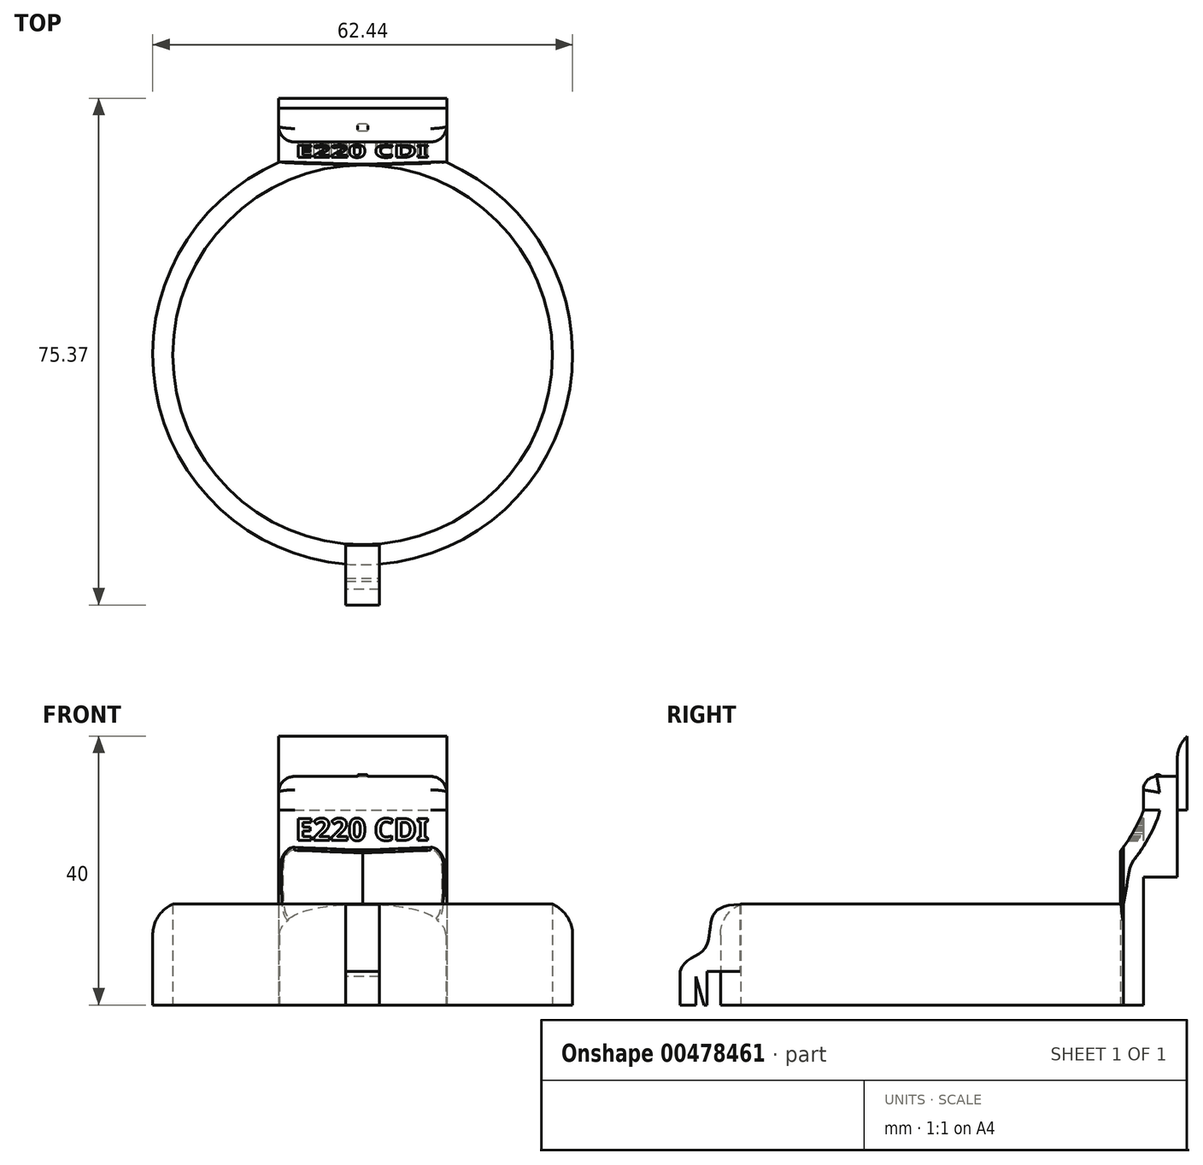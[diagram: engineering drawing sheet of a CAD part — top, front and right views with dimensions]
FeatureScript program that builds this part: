
annotation { "Feature Type Name" : "Feature", "Feature Type Description" : "" }
export const myFeature = defineFeature(function(context is Context, id is Id, definition is map)
    precondition{}
    {
        {
            var Q0;
            Q0=qCreatedBy(makeId("Top.planeOp"),FACE);
            var sketch = newSketch(context, id + "F0", { "sketchPlane" : qUnion([Q0])});
            skCircle(sketch, "E0", {"center": v(0, 0) * mm, "radius": 28.22 * mm});
            skCircle(sketch, "E1", {"center": v(0, 0) * mm, "radius": 31.22 * mm});
            skPoint(sketch, "E2", {"position": v(0, 31.22) * mm});
            skSolve(sketch);
        }
        {
            var Q0;
            Q0=makeQuery(id+"F0.imprint","IMPRINT",FACE,{"disambiguationData":[TD([[makeQuery(id+"F0.imprint","IMPRINT",EDGE,{"derivedFrom":sQuery(id+"F0.wireOp",EDGE,"E0")}),-1.0]])]});
            extrude(context, id + "F1", {"entities" : qUnion([Q0]), "depth" : 10 * mm, "hasSecondDirection" : true, "secondDirectionOppositeDirection" : true, "secondDirectionDepth" : 5 * mm});
        }
        {
            var Q0;
            Q0=qCreatedBy(makeId("Top.planeOp"),FACE);
            var sketch = newSketch(context, id + "F2", { "sketchPlane" : qUnion([Q0])});
            skLineSegment(sketch, "E3.bottom", {"start": v(-12.5, 31.66) * mm, "end": v(12.5, 31.66) * mm});
            skLineSegment(sketch, "E3.top", {"start": v(-12.5, 28.66) * mm, "end": v(12.5, 28.66) * mm});
            skLineSegment(sketch, "E3.left", {"start": v(-12.5, 31.66) * mm, "end": v(-12.5, 28.66) * mm});
            skLineSegment(sketch, "E3.right", {"start": v(12.5, 31.66) * mm, "end": v(12.5, 28.66) * mm});
            skLineSegment(sketch, "E4", {"start": v(-12.5, 31.66) * mm, "end": v(12.5, 28.66) * mm, "construction": true});
            skLineSegment(sketch, "E5", {"start": v(-12.5, 28.66) * mm, "end": v(12.5, 31.66) * mm, "construction": true});
            skPoint(sketch, "E6", {"position": v(0, 30.16) * mm});
            skSolve(sketch);
        }
        {
            var Q0;
            Q0=qSketchRegion(id+"F2",true);
            extrude(context, id + "F3", {"entities" : qUnion([Q0]), "operationType" : NewBodyOperationType.ADD, "depth" : 24 * mm, "hasSecondDirection" : true, "secondDirectionOppositeDirection" : true, "secondDirectionDepth" : 5 * mm});
        }
        {
            var Q0;
            Q0=makeQuery(id+"F3.opExtrude","CAP_FACE",FACE,{"disambiguationData":[OSD([sQuery(id+"F2.wireOp",EDGE,"E3.bottom"),sQuery(id+"F2.wireOp",EDGE,"E3.top"),sQuery(id+"F2.wireOp",EDGE,"E3.left"),sQuery(id+"F2.wireOp",EDGE,"E3.right")])],"isStart":false});
            var sketch = newSketch(context, id + "F4", { "sketchPlane" : qUnion([Q0])});
            skLineSegment(sketch, "E7.bottom", {"start": v(-12.5, 31.66) * mm, "end": v(12.5, 31.66) * mm});
            skLineSegment(sketch, "E7.top", {"start": v(-12.5, 36.66) * mm, "end": v(12.5, 36.66) * mm});
            skLineSegment(sketch, "E7.left", {"start": v(-12.5, 31.66) * mm, "end": v(-12.5, 36.66) * mm});
            skLineSegment(sketch, "E7.right", {"start": v(12.5, 31.66) * mm, "end": v(12.5, 36.66) * mm});
            skSolve(sketch);
        }
        {
            var Q0;
            Q0=qSketchRegion(id+"F4",true);
            extrude(context, id + "F5", {"entities" : qUnion([Q0]), "operationType" : NewBodyOperationType.ADD, "oppositeDirection" : true, "depth" : 10 * mm, "hasSecondDirection" : true, "secondDirectionOppositeDirection" : false, "secondDirectionDepth" : 5 * mm});
        }
        {
            var Q0;
            Q0=makeQuery(id+"F5.opExtrude","CAP_FACE",FACE,{"disambiguationData":[OSD([sQuery(id+"F4.wireOp",EDGE,"E7.bottom"),sQuery(id+"F4.wireOp",EDGE,"E7.top"),sQuery(id+"F4.wireOp",EDGE,"E7.left"),sQuery(id+"F4.wireOp",EDGE,"E7.right")])],"isStart":true});
            var sketch = newSketch(context, id + "F6", { "sketchPlane" : qUnion([Q0])});
            skLineSegment(sketch, "E8.bottom", {"start": v(-12.5, 36.66) * mm, "end": v(12.51, 36.66) * mm});
            skLineSegment(sketch, "E8.top", {"start": v(-12.5, 38.17) * mm, "end": v(12.51, 38.17) * mm});
            skLineSegment(sketch, "E8.left", {"start": v(-12.5, 36.66) * mm, "end": v(-12.5, 38.17) * mm});
            skLineSegment(sketch, "E8.right", {"start": v(12.51, 36.66) * mm, "end": v(12.51, 38.17) * mm});
            skSolve(sketch);
        }
        {
            var Q0;
            Q0=qCreatedBy(makeId("Right.planeOp"),FACE);
            var sketch = newSketch(context, id + "F7", { "sketchPlane" : qUnion([Q0])});
            skFitSpline(sketch, "E9", {"points": [v(-37.2, 0) * mm, v(-33.61, 3.33) * mm, v(-32.43, 8.1) * mm, v(-28.31, 9.98) * mm], "startDerivative": vector(3.1, 16.24) * mm, "endDerivative": vector(22.01, 0.89) * mm});
            skLineSegment(sketch, "E10", {"start": v(-28.31, 9.98) * mm, "end": v(-28.31, 0) * mm});
            skLineSegment(sketch, "E11", {"start": v(-28.31, 0) * mm, "end": v(-37.2, 0) * mm});
            skSolve(sketch);
        }
        {
            var Q0;
            Q0=makeQuery(id+"F7.imprint","IMPRINT",FACE,{"disambiguationData":[TD([[makeQuery(id+"F7.imprint","IMPRINT",EDGE,{"derivedFrom":sQuery(id+"F7.wireOp",EDGE,"E9")}),-1.0]])]});
            extrude(context, id + "F8", {"entities" : qUnion([Q0]), "depth" : 2.5 * mm, "hasSecondDirection" : true, "secondDirectionOppositeDirection" : true, "secondDirectionDepth" : 2.5 * mm});
        }
        {
            var Q0;
            Q0=qCreatedBy(makeId("Top.planeOp"),FACE);
            var sketch = newSketch(context, id + "F9", { "sketchPlane" : qUnion([Q0])});
            skLineSegment(sketch, "E12.bottom", {"start": v(-2.5, -37.2) * mm, "end": v(2.5, -37.2) * mm});
            skLineSegment(sketch, "E12.top", {"start": v(-2.5, -33.2) * mm, "end": v(2.5, -33.2) * mm});
            skLineSegment(sketch, "E12.left", {"start": v(-2.5, -37.2) * mm, "end": v(-2.5, -33.2) * mm});
            skLineSegment(sketch, "E12.right", {"start": v(2.5, -37.2) * mm, "end": v(2.5, -33.2) * mm});
            skSolve(sketch);
        }
        {
            var Q0;
            Q0=qSketchRegion(id+"F9",true);
            extrude(context, id + "F10", {"entities" : qUnion([Q0]), "operationType" : NewBodyOperationType.ADD, "oppositeDirection" : true, "depth" : 5 * mm});
        }
        {
            var Q0;
            {var subQ0=sQuery(id+"F0.wireOp",EDGE,"E1");var subQ1=sQuery(id+"F0.wireOp",EDGE,"E0");Q0=makeQuery(id+"F3.boolean.opBoolean","SPLIT",FACE,{"disambiguationData":[TD([makeQuery(id+"F1.opExtrude","SWEPT_FACE",FACE,{"disambiguationData":[OSD([subQ1])]})])],"derivedFrom":makeQuery(id+"F1.opExtrude","CAP_FACE",FACE,{"disambiguationData":[OSD([subQ1,subQ0])],"isStart":false})});}
            var sketch = newSketch(context, id + "F11", { "sketchPlane" : qUnion([Q0])});
            skFitSpline(sketch, "E13", {"points": [v(-12.37, 28.66) * mm, v(-7.02, 28.42) * mm, v(0, 28.22) * mm], "startDerivative": vector(16.95, -1.43) * mm, "endDerivative": vector(20.26, -0.24) * mm});
            skLineSegment(sketch, "E14", {"start": v(0, 28.22) * mm, "end": v(0, 28.66) * mm});
            skLineSegment(sketch, "E15", {"start": v(0, 28.66) * mm, "end": v(-12.37, 28.66) * mm});
            skFitSpline(sketch, "E16.MirrorCS", {"points": [v(12.37, 28.66) * mm, v(7.02, 28.42) * mm, v(0, 28.22) * mm], "startDerivative": vector(-16.95, -1.43) * mm, "endDerivative": vector(-20.26, -0.24) * mm});
            skLineSegment(sketch, "E17.MirrorCS", {"start": v(0, 28.66) * mm, "end": v(12.37, 28.66) * mm});
            skSolve(sketch);
        }
        {
            var Q0;
            Q0=qSketchRegion(id+"F11",true);
            extrude(context, id + "F12", {"entities" : qUnion([Q0]), "operationType" : NewBodyOperationType.ADD, "depth" : 14 * mm});
        }
        {
            var Q0;
            Q0=makeQuery(id+"F6.imprint","IMPRINT",FACE,{"disambiguationData":[TD([[makeQuery(id+"F6.imprint","IMPRINT",EDGE,{"derivedFrom":sQuery(id+"F6.wireOp",EDGE,"E8.top")}),-1.0]])]});
            extrude(context, id + "F13", {"entities" : qUnion([Q0]), "operationType" : NewBodyOperationType.ADD, "depth" : 6 * mm, "hasSecondDirection" : true, "secondDirectionOppositeDirection" : true, "secondDirectionDepth" : 5 * mm});
        }
        {
            var Q0;
            Q0=makeQuery(id+"F13.opExtrude","CAP_EDGE",EDGE,{"disambiguationData":[OSD([sQuery(id+"F6.wireOp",EDGE,"E8.bottom")])],"isStart":false});
            fillet(context, id + "F14", {"entities" : qUnion([Q0]), "radius" : 5 * mm, "tangentPropagation" : true, "allowEdgeOverflow" : false});
        }
        {
            var Q0;
            Q0=qCreatedBy(makeId("Right.planeOp"),FACE);
            var sketch = newSketch(context, id + "F15", { "sketchPlane" : qUnion([Q0])});
            skFitSpline(sketch, "E18", {"points": [v(31.66, 24) * mm, v(29.11, 19.07) * mm, v(27.3, 15.86) * mm, v(25.83, 10.1) * mm, v(23.5, 28.91) * mm, v(28.8, 25.36) * mm], "startDerivative": vector(-0.11, -8.56) * mm, "endDerivative": vector(26.45, -28.76) * mm});
            skLineSegment(sketch, "E19", {"start": v(28.8, 25.36) * mm, "end": v(31.66, 24) * mm});
            skSolve(sketch);
        }
        {
            var Q0;
            Q0 = qSketchRegion(id + "F15", true);
            extrude(context, id + "F16", {"entities" : qUnion([Q0]), "operationType" : NewBodyOperationType.REMOVE, "endBound" : BoundingType.THROUGH_ALL, "oppositeDirection" : true, "depth" : 25 * mm, "hasSecondDirection" : true, "secondDirectionBound" : SecondDirectionBoundingType.THROUGH_ALL, "secondDirectionOppositeDirection" : false, "secondDirectionDepth" : 25 * mm});
        }
        {
            var Q0;
            Q0=qCreatedBy(makeId("Right.planeOp"),FACE);
            var sketch = newSketch(context, id + "F17", { "sketchPlane" : qUnion([Q0])});
            skArc(sketch, "E20", {"start": v(34.37, 28.94) * mm, "mid": v(33.81, 29.28) * mm, "end": v(33.26, 28.94) * mm});
            skLineSegment(sketch, "E21", {"start": v(33.26, 28.94) * mm, "end": v(34.37, 28.94) * mm});
            skSolve(sketch);
        }
        {
            var Q0;
            Q0=makeQuery(id+"F17.imprint","IMPRINT",FACE,{"disambiguationData":[TD([[makeQuery(id+"F17.imprint","IMPRINT",EDGE,{"derivedFrom":sQuery(id+"F17.wireOp",EDGE,"E20")}),1.0]])]});
            var Q1;
            Q1 = qConstructionFilter(qBodyType(qCreatedBy(id + "F17" ,EDGE), BodyType.WIRE), ConstructionObject.NO);
            extrude(context, id + "F18", {"entities" : qUnion([Q0]), "surfaceEntities" : qUnion([Q1]), "endBound" : BoundingType.SYMMETRIC, "depth" : 1.5 * mm});
        }
        {
            var Q0;
            Q0=makeQuery(id+"F18.opExtrude","CAP_EDGE",EDGE,{"disambiguationData":[OSD([sQuery(id+"F17.wireOp",EDGE,"E20")])],"isStart":true});
            var Q1;
            Q1=makeQuery(id+"F18.opExtrude","CAP_EDGE",EDGE,{"disambiguationData":[OSD([sQuery(id+"F17.wireOp",EDGE,"E20")])],"isStart":false});
            fillet(context, id + "F19", {"entities" : qUnion([Q0, Q1]), "radius" : 0.22 * mm, "tangentPropagation" : true, "allowEdgeOverflow" : false});
        }
        {
            var Q0;
            Q0=makeQuery(id+"F5.opExtrude","CAP_EDGE",EDGE,{"disambiguationData":[OSD([sQuery(id+"F4.wireOp",EDGE,"E7.bottom")])],"isStart":true});
            fillet(context, id + "F20", {"entities" : qUnion([Q0]), "radius" : 2 * mm, "tangentPropagation" : true, "allowEdgeOverflow" : false});
        }
        {
            var Q0;
            Q0=makeQuery(id+"F16.boolean.opBoolean","INTERSECT",EDGE,{"derivedFrom":[makeQuery(id+"F5.boolean.opBoolean","MERGE",FACE,{"derivedFrom":[makeQuery(id+"F3.opExtrude","SWEPT_FACE",FACE,{"disambiguationData":[OSD([sQuery(id+"F2.wireOp",EDGE,"E3.right")])]}),makeQuery(id+"F5.opExtrude","SWEPT_FACE",FACE,{"disambiguationData":[OSD([sQuery(id+"F4.wireOp",EDGE,"E7.right")])]})]}),makeQuery(id+"F16.opExtrude","SWEPT_FACE",FACE,{"disambiguationData":[OSD([sQuery(id+"F15.wireOp",EDGE,"E18")])]})]});
            var Q1;
            Q1=makeQuery(id+"F5.opExtrude","SWEPT_EDGE",EDGE,{"disambiguationData":[OSD([sQuery(id+"F2.wireOp",EDGE,"E3.right"),sQuery(id+"F4.wireOp",EDGE,"E7.bottom"),sQuery(id+"F4.wireOp",EDGE,"E7.right")])]});
            var Q2;
            Q2=makeQuery(id+"F5.opExtrude","SWEPT_EDGE",EDGE,{"disambiguationData":[OSD([sQuery(id+"F2.wireOp",EDGE,"E3.left"),sQuery(id+"F4.wireOp",EDGE,"E7.bottom"),sQuery(id+"F4.wireOp",EDGE,"E7.left")])]});
            var Q3;
            Q3=makeQuery(id+"F16.boolean.opBoolean","INTERSECT",EDGE,{"derivedFrom":[makeQuery(id+"F13.boolean.opBoolean","MERGE",FACE,{"derivedFrom":[makeQuery(id+"F5.boolean.opBoolean","MERGE",FACE,{"derivedFrom":[makeQuery(id+"F3.opExtrude","SWEPT_FACE",FACE,{"disambiguationData":[OSD([sQuery(id+"F2.wireOp",EDGE,"E3.left")])]}),makeQuery(id+"F5.opExtrude","SWEPT_FACE",FACE,{"disambiguationData":[OSD([sQuery(id+"F4.wireOp",EDGE,"E7.left")])]})]}),makeQuery(id+"F13.opExtrude","SWEPT_FACE",FACE,{"disambiguationData":[OSD([sQuery(id+"F6.wireOp",EDGE,"E8.left")])]})]}),makeQuery(id+"F16.opExtrude","SWEPT_FACE",FACE,{"disambiguationData":[OSD([sQuery(id+"F15.wireOp",EDGE,"E18")])]})]});
            fillet(context, id + "F21", {"entities" : qUnion([Q0, Q1, Q2, Q3]), "radius" : 2.4 * mm, "tangentPropagation" : true, "allowEdgeOverflow" : false});
        }
        {
            var Q0;
            {var subQ0=sQuery(id+"F0.wireOp",EDGE,"E1");Q0=makeQuery(id+"F3.boolean.opBoolean","SPLIT",EDGE,{"disambiguationData":[TD([makeQuery(id+"F3.opExtrude","SWEPT_FACE",FACE,{"disambiguationData":[OSD([sQuery(id+"F2.wireOp",EDGE,"E3.top")])]})])],"derivedFrom":makeQuery(id+"F1.opExtrude","CAP_EDGE",EDGE,{"disambiguationData":[OSD([subQ0])],"isStart":false})});}
            fillet(context, id + "F22", {"entities" : qUnion([Q0]), "radius" : 5 * mm, "tangentPropagation" : true, "allowEdgeOverflow" : false});
        }
        {
            var Q0;
            Q0=makeQuery(id+"F10.opExtrude","SWEPT_FACE",FACE,{"disambiguationData":[OSD([sQuery(id+"F9.wireOp",EDGE,"E12.left")])]});
            var sketch = newSketch(context, id + "F23", { "sketchPlane" : qUnion([Q0])});
            skLineSegment(sketch, "E22", {"start": v(33.55, -5.5) * mm, "end": v(34.9, -0.74) * mm});
            skLineSegment(sketch, "E23", {"start": v(34.9, -0.74) * mm, "end": v(34.9, -5.72) * mm});
            skLineSegment(sketch, "E24", {"start": v(34.9, -5.72) * mm, "end": v(33.55, -5.5) * mm});
            skSolve(sketch);
        }
        {
            var Q0;
            Q0 = qSketchRegion(id + "F23", true);
            extrude(context, id + "F24", {"entities" : qUnion([Q0]), "operationType" : NewBodyOperationType.REMOVE, "endBound" : BoundingType.THROUGH_ALL, "oppositeDirection" : true, "depth" : 25 * mm});
        }
        {
            var Q0;
            Q0=makeQuery(id+"F5.opExtrude","SWEPT_FACE",FACE,{"disambiguationData":[OSD([sQuery(id+"F4.wireOp",EDGE,"E7.bottom")])]});
            var sketch = newSketch(context, id + "F25", { "sketchPlane" : qUnion([Q0])});
            skText(sketch, "E25", { "text": "E220 CDI", "fontName": "NotoSans-Bold.ttf"});
            const initialGuessF25  = {"E25": [-0.01, 0.01946, 1, 0, 0.00332]};
            skSetInitialGuess(sketch, initialGuessF25);
            skSolve(sketch);
        }
        {
            var Q0;
            Q0 = qSketchRegion(id + "F25", true);
            extrude(context, id + "F26", {"entities" : qUnion([Q0]), "operationType" : NewBodyOperationType.REMOVE, "depth" : 3 * mm});
        }
        {
            var Q0;
            Q0=makeQuery(id+"F16.boolean.opBoolean","INTERSECT",EDGE,{"derivedFrom":[makeQuery(id+"F12.opExtrude","SWEPT_FACE",FACE,{"disambiguationData":[OSD([sQuery(id+"F11.wireOp",EDGE,"E16.MirrorCS")])]}),makeQuery(id+"F16.opExtrude","SWEPT_FACE",FACE,{"disambiguationData":[OSD([sQuery(id+"F15.wireOp",EDGE,"E18")])]})]});
            var Q1;
            Q1=makeQuery(id+"F16.boolean.opBoolean","INTERSECT",EDGE,{"derivedFrom":[makeQuery(id+"F12.opExtrude","SWEPT_FACE",FACE,{"disambiguationData":[OSD([sQuery(id+"F11.wireOp",EDGE,"E13")])]}),makeQuery(id+"F16.opExtrude","SWEPT_FACE",FACE,{"disambiguationData":[OSD([sQuery(id+"F15.wireOp",EDGE,"E18")])]})]});
            fillet(context, id + "F27", {"entities" : qUnion([Q0, Q1]), "radius" : 0.7 * mm, "tangentPropagation" : true, "allowEdgeOverflow" : false});
        }
    });
